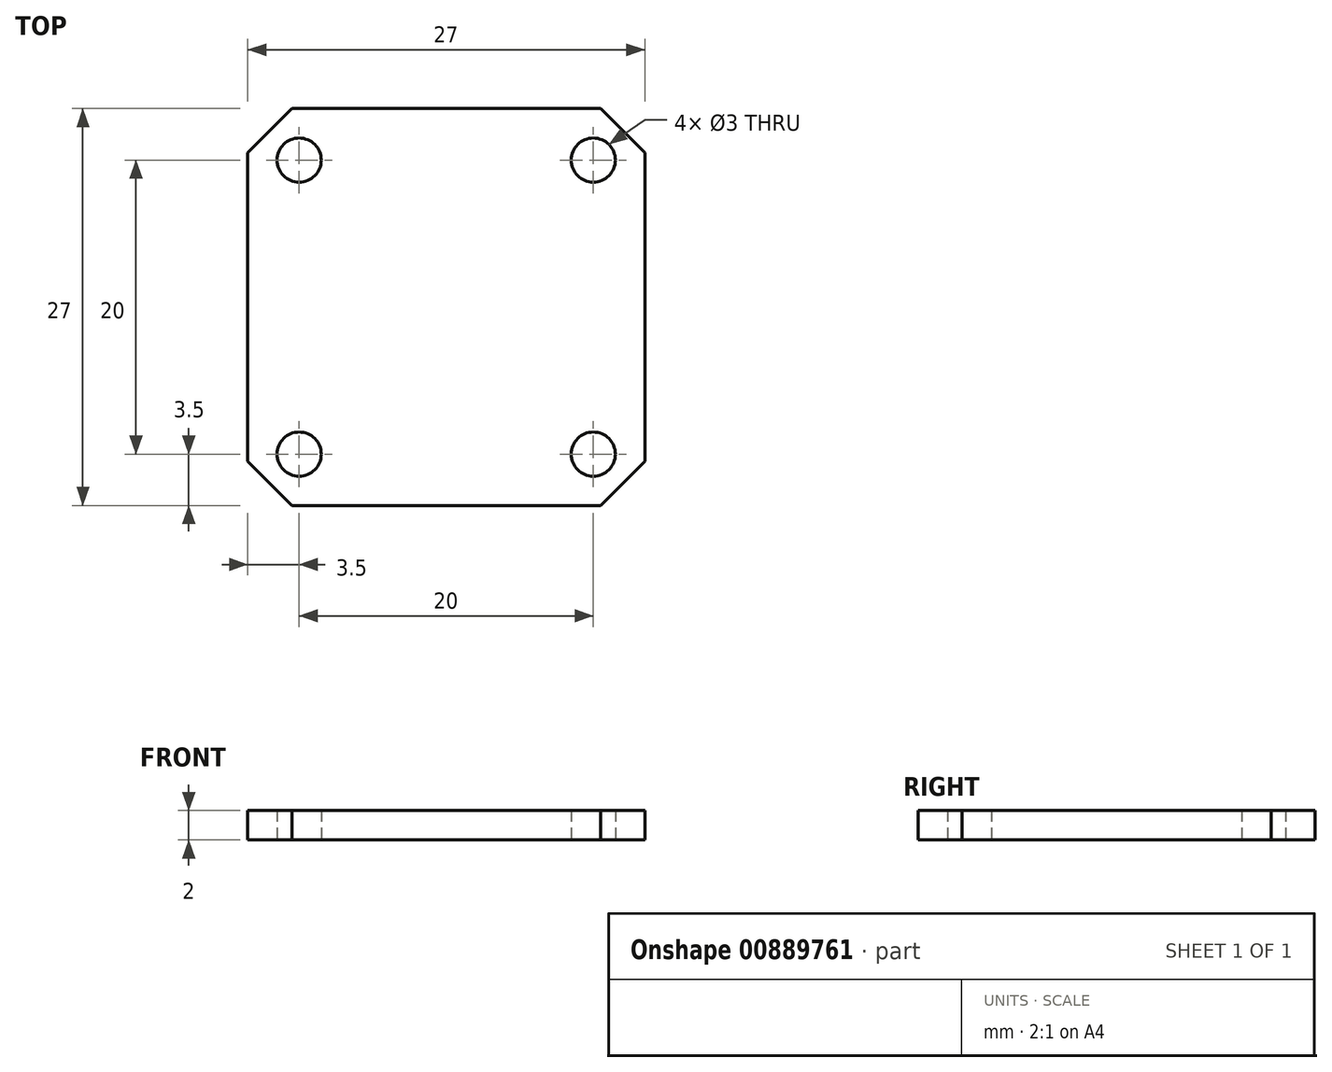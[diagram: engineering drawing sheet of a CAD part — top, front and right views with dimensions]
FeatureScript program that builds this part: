
annotation { "Feature Type Name" : "Feature", "Feature Type Description" : "" }
export const myFeature = defineFeature(function(context is Context, id is Id, definition is map)
    precondition{}
    {
        {
            var Q0;
            Q0=qCreatedBy(makeId("Top.planeOp"),FACE);
            var sketch = newSketch(context, id + "F0", { "sketchPlane" : qUnion([Q0])});
            skLineSegment(sketch, "E0.bottom", {"start": v(-13.5, 13.5) * mm, "end": v(13.5, 13.5) * mm});
            skLineSegment(sketch, "E0.top", {"start": v(-13.5, -13.5) * mm, "end": v(13.5, -13.5) * mm});
            skLineSegment(sketch, "E0.left", {"start": v(-13.5, 13.5) * mm, "end": v(-13.5, -13.5) * mm});
            skLineSegment(sketch, "E0.right", {"start": v(13.5, 13.5) * mm, "end": v(13.5, -13.5) * mm});
            skCircle(sketch, "E1", {"center": v(-10, 10) * mm, "radius": 1.5 * mm});
            skLineSegment(sketch, "E2", {"start": v(-13.5, -13.5) * mm, "end": v(13.5, 13.5) * mm, "construction": true});
            skCircle(sketch, "E3.1.0", {"center": v(-10, -10) * mm, "radius": 1.5 * mm});
            skCircle(sketch, "E3.2.0", {"center": v(10, -10) * mm, "radius": 1.5 * mm});
            skCircle(sketch, "E3.3.0", {"center": v(10, 10) * mm, "radius": 1.5 * mm});
            skPoint(sketch, "E3.center", {"position": v(0, 0) * mm});
            skSolve(sketch);
        }
        {
            var Q0;
            Q0=qSketchRegion(id+"F0",true);
            extrude(context, id + "F1", {"entities" : qUnion([Q0]), "depth" : 2 * mm});
        }
        {
            var Q0;
            Q0=makeQuery(id+"F1.opExtrude","SWEPT_EDGE",EDGE,{"disambiguationData":[OSD([sQuery(id+"F0.wireOp",EDGE,"E0.top"),sQuery(id+"F0.wireOp",EDGE,"E0.right")])]});
            var Q1;
            Q1=makeQuery(id+"F1.opExtrude","SWEPT_EDGE",EDGE,{"disambiguationData":[OSD([sQuery(id+"F0.wireOp",EDGE,"E0.top"),sQuery(id+"F0.wireOp",EDGE,"E0.left")])]});
            var Q2;
            Q2=makeQuery(id+"F1.opExtrude","SWEPT_EDGE",EDGE,{"disambiguationData":[OSD([sQuery(id+"F0.wireOp",EDGE,"E0.bottom"),sQuery(id+"F0.wireOp",EDGE,"E0.right")])]});
            var Q3;
            Q3=makeQuery(id+"F1.opExtrude","SWEPT_EDGE",EDGE,{"disambiguationData":[OSD([sQuery(id+"F0.wireOp",EDGE,"E0.bottom"),sQuery(id+"F0.wireOp",EDGE,"E0.left")])]});
            chamfer(context, id + "F2", {"entities" : qUnion([Q0, Q1, Q2, Q3]), "width" : 3 * mm, "tangentPropagation" : true});
        }
    });
